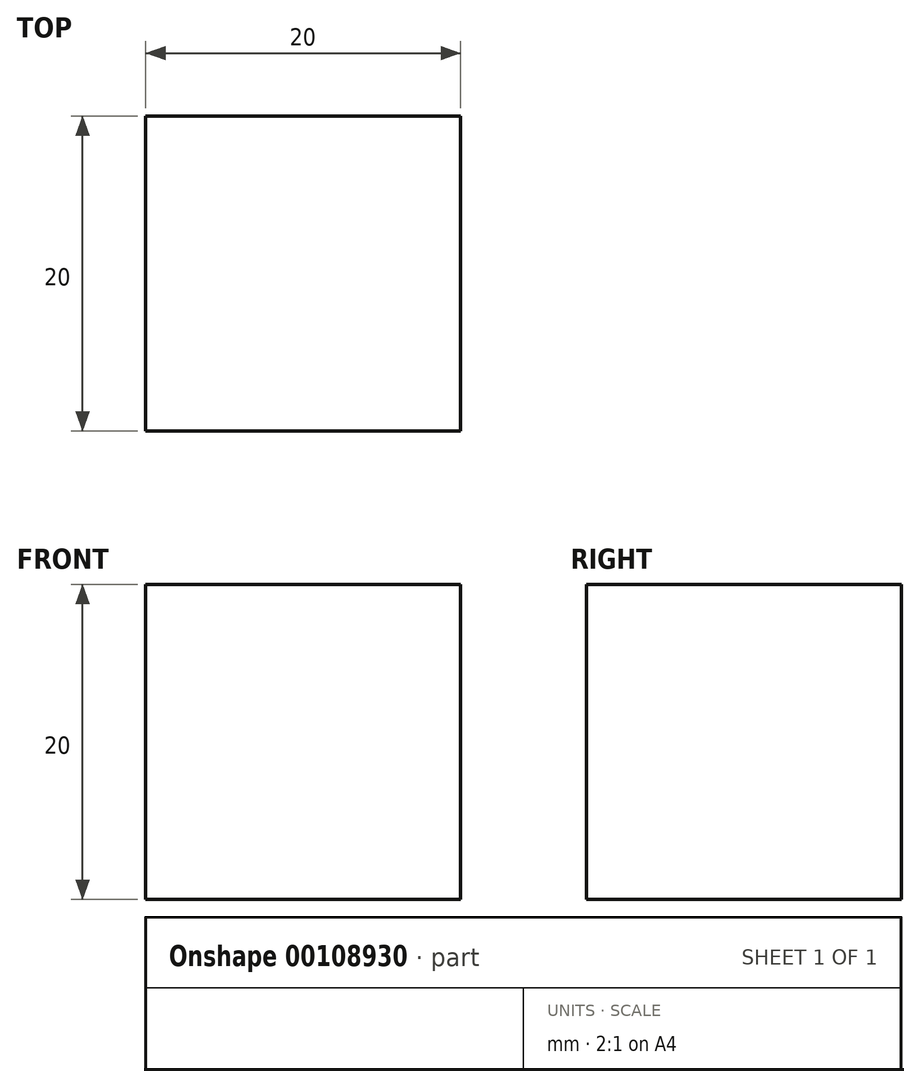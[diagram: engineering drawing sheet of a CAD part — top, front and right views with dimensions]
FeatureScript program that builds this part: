
annotation { "Feature Type Name" : "Feature", "Feature Type Description" : "" }
export const myFeature = defineFeature(function(context is Context, id is Id, definition is map)
    precondition{}
    {
        {
            var Q0;
            Q0=qCreatedBy(makeId("Top.planeOp"),FACE);
            var sketch = newSketch(context, id + "F0", { "sketchPlane" : qUnion([Q0])});
            skLineSegment(sketch, "E0.bottom", {"start": v(10, -10) * mm, "end": v(-10, -10) * mm});
            skLineSegment(sketch, "E0.top", {"start": v(10, 10) * mm, "end": v(-10, 10) * mm});
            skLineSegment(sketch, "E0.left", {"start": v(10, -10) * mm, "end": v(10, 10) * mm});
            skLineSegment(sketch, "E0.right", {"start": v(-10, -10) * mm, "end": v(-10, 10) * mm});
            skPoint(sketch, "E0.middle", {"position": v(0, 0) * mm});
            skSolve(sketch);
        }
        {
            var Q0;
            Q0 = qSketchRegion(id + "F0", true);
            extrude(context, id + "F1", {"entities" : qUnion([Q0]), "endBound" : BoundingType.SYMMETRIC, "depth" : 20 * mm});
        }
    });
